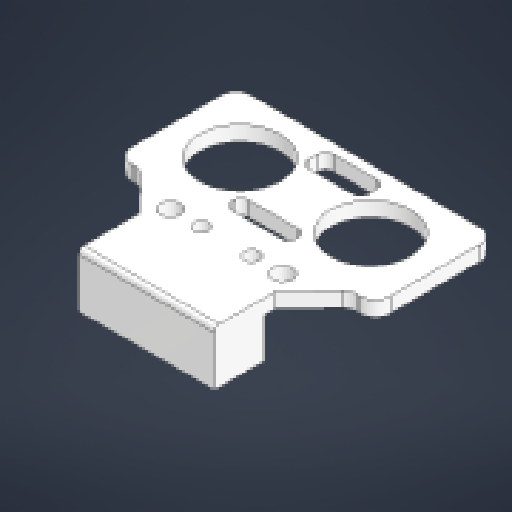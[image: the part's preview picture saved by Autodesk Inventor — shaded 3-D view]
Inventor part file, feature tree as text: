
AUTODESK INVENTOR PART (.ipt)
format: ipt  version: 2023 (Build 270158000, 158)  size: 309,248 bytes
history: mixed  units: in
note: dims shown in document units (in); Inventor stores cm internally (conversion verified against a paired STEP export)
features: extrude x5, sketch x5, other x3, fillet x2, projected_geometry x2, reference x2, imported_body x1
ambient origin geometry x8: Origin, YZ Plane, XZ Plane, XY Plane, X Axis, Y Axis, Z Axis, Center Point
bodies: Solid1 (imported_parasolid)
feature tree (20):
  extrude  "Extrusion1"  Depth=0.4813in TaperAngle=0.0deg
  extrude  "Extrusion2"  Depth=0.1181in TaperAngle=0.0deg
  fillet  "Fillet2"  Radius=0.003in
  extrude  "Extrusion3"  Depth=0.315in TaperAngle=0.0deg
  sketch  "Sketch5"  dims[d23=0.003in d24=0.003in]
  extrude  "Extrusion5"  Depth=0.003in
  extrude  "Extrusion6"  [1 undecoded]
  sketch  "Sketch1"  dims[d0=0.4813in d1=0.0in d2=0.4813in d3=0.0in]
  sketch  "Sketch2"  dims[d13=0.0394in d14=0.1181in d15=0.0in d16=0.003in]
  projected_geometry  "Projected Loop1"
  sketch  "Sketch4"  dims[d20=0.3937in d21=0.315in d22=0.0in]
  reference  "Reference1"
  reference  "Reference2"
  sketch  "Sketch6"  dims[d25=0.3937in d26=0.0in]
  projected_geometry  "Projected Loop2"
  fillet  "Fillet1"  [1 undecoded]
  other  "<userpath>\Documents\GitHub\SDP-Kepler-1708b\FlyingUGV.iam"
  other  "FlyingUGV.iam"
  other  "HC-SR04-UltrasonicSensor v7:1"
  imported_body  NMx_Import_Brep_tag  [imported B-rep: ~43 faces, bbox_mm=[52.0, 11.0, 44.0]]
note: 2 required parameter values undecoded (feature->parameter linkage not recoverable at this tier; creation-order binding heuristic only, values carry confidence <= 0.55)
